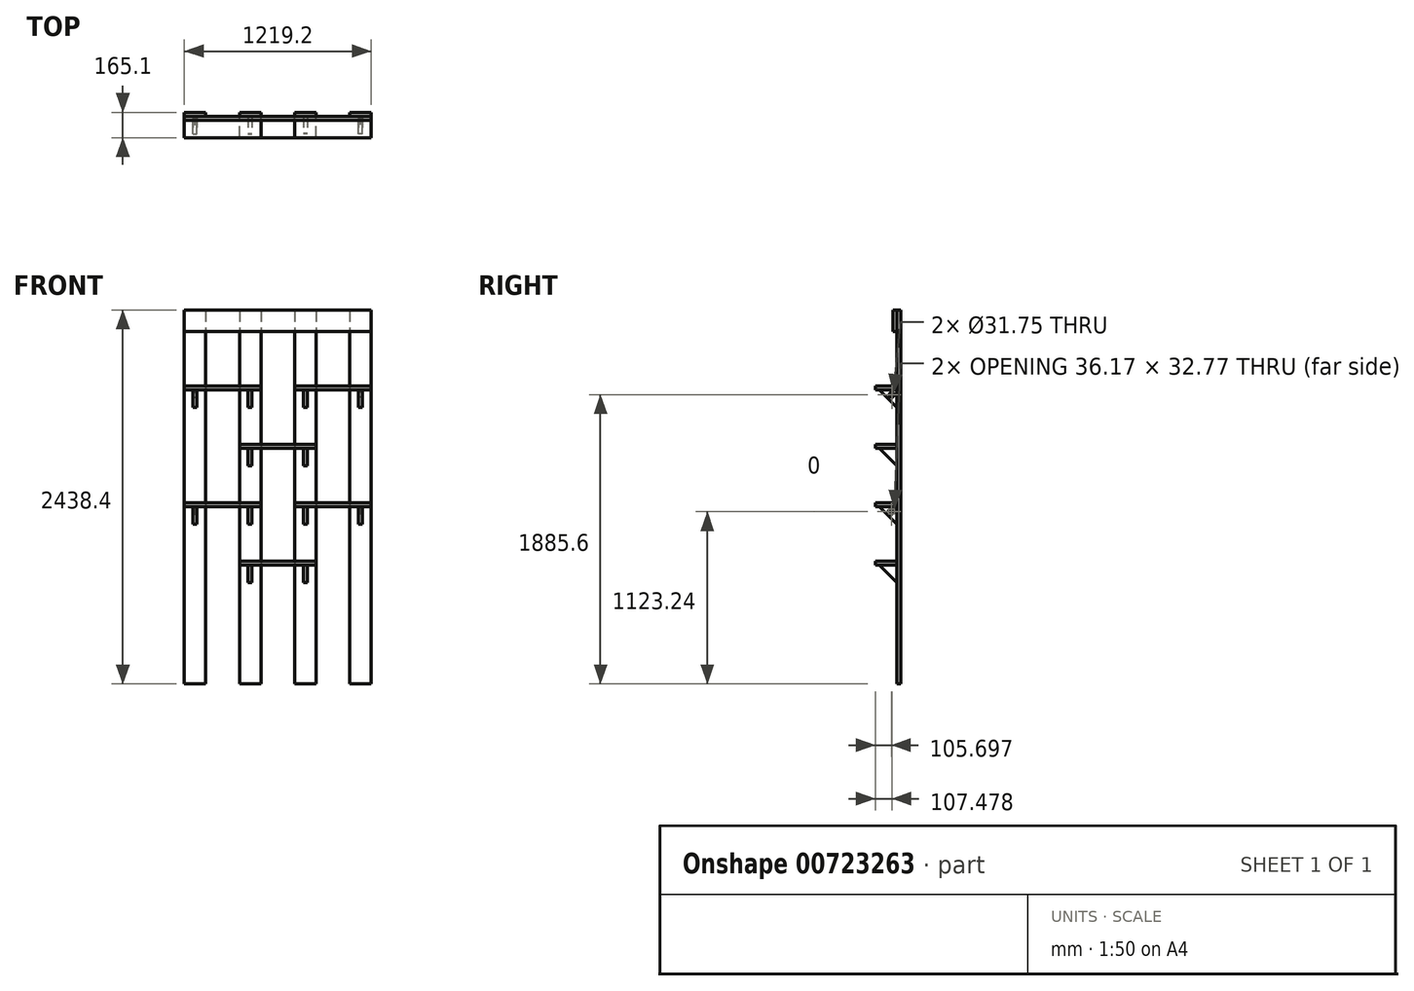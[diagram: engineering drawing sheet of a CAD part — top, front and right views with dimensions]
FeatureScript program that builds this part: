
annotation { "Feature Type Name" : "Feature", "Feature Type Description" : "" }
export const myFeature = defineFeature(function(context is Context, id is Id, definition is map)
    precondition{}
    {
        {
            var Q0;
            Q0=qCreatedBy(makeId("Front.planeOp"),FACE);
            var Q1;
            Q1 = qBodyType(qCreatedBy(id + "F1" ,EDGE), BodyType.WIRE);
            cPlane(context, id + "F0", {"entities" : qUnion([Q0, Q1]), "cplaneType" : CPlaneType.OFFSET, "offset" : 25.4 * mm, "width" : 152.4 * mm, "height" : 152.4 * mm});
        }
        {
            var Q0;
            Q0=qCreatedBy(id+"F0.planeOp",FACE);
            var sketch = newSketch(context, id + "F1", { "sketchPlane" : qUnion([Q0])});
            skLineSegment(sketch, "E0.bottom", {"start": v(-609.6, 139.7) * mm, "end": v(609.6, 139.7) * mm});
            skLineSegment(sketch, "E0.top", {"start": v(-609.6, 0) * mm, "end": v(609.6, 0) * mm});
            skLineSegment(sketch, "E0.left", {"start": v(-609.6, 139.7) * mm, "end": v(-609.6, 0) * mm});
            skLineSegment(sketch, "E0.right", {"start": v(609.6, 139.7) * mm, "end": v(609.6, 0) * mm});
            skPoint(sketch, "E1", {"position": v(0, 0) * mm});
            skSolve(sketch);
        }
        {
            var Q0;
            Q0=qCreatedBy(makeId("Front.planeOp"),FACE);
            var sketch = newSketch(context, id + "F2", { "sketchPlane" : qUnion([Q0])});
            skLineSegment(sketch, "E2.bottom", {"start": v(-609.6, 139.7) * mm, "end": v(-469.9, 139.7) * mm});
            skLineSegment(sketch, "E2.top", {"start": v(-609.6, -2298.7) * mm, "end": v(-469.9, -2298.7) * mm});
            skLineSegment(sketch, "E2.left", {"start": v(-609.6, 139.7) * mm, "end": v(-609.6, -2298.7) * mm});
            skLineSegment(sketch, "E2.right", {"start": v(-469.9, 139.7) * mm, "end": v(-469.9, -2298.7) * mm});
            skLineSegment(sketch, "E3", {"start": v(304.8, 139.7) * mm, "end": v(304.8, -1993.9) * mm, "construction": true});
            skLineSegment(sketch, "E4.MirrorCS", {"start": v(0.57, 139.7) * mm, "end": v(0.57, -1993.9) * mm, "construction": true});
            skLineSegment(sketch, "E5.bottom", {"start": v(110.24, 139.7) * mm, "end": v(249.94, 139.7) * mm});
            skLineSegment(sketch, "E5.top", {"start": v(110.24, -2298.7) * mm, "end": v(249.94, -2298.7) * mm});
            skLineSegment(sketch, "E5.left", {"start": v(110.24, 139.7) * mm, "end": v(110.24, -2298.7) * mm});
            skLineSegment(sketch, "E5.right", {"start": v(249.94, 139.7) * mm, "end": v(249.94, -2298.7) * mm});
            skLineSegment(sketch, "E6.bottom", {"start": v(469.9, 139.7) * mm, "end": v(609.6, 139.7) * mm});
            skLineSegment(sketch, "E6.top", {"start": v(469.9, -2298.7) * mm, "end": v(609.6, -2298.7) * mm});
            skLineSegment(sketch, "E6.left", {"start": v(469.9, 139.7) * mm, "end": v(469.9, -2298.7) * mm});
            skLineSegment(sketch, "E6.right", {"start": v(609.6, 139.7) * mm, "end": v(609.6, -2298.7) * mm});
            skLineSegment(sketch, "E7.bottom", {"start": v(-249.68, 139.7) * mm, "end": v(-109.98, 139.7) * mm});
            skLineSegment(sketch, "E7.top", {"start": v(-249.68, -2298.7) * mm, "end": v(-109.98, -2298.7) * mm});
            skLineSegment(sketch, "E7.left", {"start": v(-249.68, 139.7) * mm, "end": v(-249.68, -2298.7) * mm});
            skLineSegment(sketch, "E7.right", {"start": v(-109.98, 139.7) * mm, "end": v(-109.98, -2298.7) * mm});
            skLineSegment(sketch, "E8.0", {"start": v(-609.6, 139.7) * mm, "end": v(609.6, 139.7) * mm, "construction": true});
            skSolve(sketch);
        }
        {
            var Q0;
            Q0 = qSketchRegion(id + "F2", true);
            extrude(context, id + "F3", {"entities" : qUnion([Q0]), "depth" : 25.4 * mm, "offsetDistance" : 25.4 * mm});
        }
        {
            var Q0;
            Q0 = qSketchRegion(id + "F1", true);
            extrude(context, id + "F4", {"entities" : qUnion([Q0]), "depth" : 25.4 * mm, "offsetDistance" : 25.4 * mm});
        }
        {
            var Q0;
            Q0=makeQuery(id+"F3.opExtrude","CAP_FACE",FACE,{"disambiguationData":[OSD([sQuery(id+"F2.wireOp",EDGE,"E2.bottom"),sQuery(id+"F2.wireOp",EDGE,"E2.top"),sQuery(id+"F2.wireOp",EDGE,"E2.left"),sQuery(id+"F2.wireOp",EDGE,"E2.right")])],"isStart":false});
            var sketch = newSketch(context, id + "F5", { "sketchPlane" : qUnion([Q0])});
            skLineSegment(sketch, "E9.bottom", {"start": v(-609.6, -355.6) * mm, "end": v(-109.98, -355.6) * mm});
            skLineSegment(sketch, "E9.top", {"start": v(-609.6, -381) * mm, "end": v(-109.98, -381) * mm});
            skLineSegment(sketch, "E9.left", {"start": v(-609.6, -355.6) * mm, "end": v(-609.6, -381) * mm});
            skLineSegment(sketch, "E9.right", {"start": v(-109.98, -355.6) * mm, "end": v(-109.98, -381) * mm});
            skLineSegment(sketch, "E10.bottom", {"start": v(-249.68, -736.6) * mm, "end": v(249.94, -736.6) * mm});
            skLineSegment(sketch, "E10.top", {"start": v(-249.68, -762) * mm, "end": v(249.94, -762) * mm});
            skLineSegment(sketch, "E10.left", {"start": v(-249.68, -736.6) * mm, "end": v(-249.68, -762) * mm});
            skLineSegment(sketch, "E10.right", {"start": v(249.94, -736.6) * mm, "end": v(249.94, -762) * mm});
            skLineSegment(sketch, "E11.bottom", {"start": v(110.24, -355.6) * mm, "end": v(609.6, -355.6) * mm});
            skLineSegment(sketch, "E11.top", {"start": v(110.24, -381) * mm, "end": v(609.6, -381) * mm});
            skLineSegment(sketch, "E11.left", {"start": v(110.24, -355.6) * mm, "end": v(110.24, -381) * mm});
            skLineSegment(sketch, "E11.right", {"start": v(609.6, -355.6) * mm, "end": v(609.6, -381) * mm});
            skLineSegment(sketch, "E12.bottom", {"start": v(-609.6, -1117.6) * mm, "end": v(-109.98, -1117.6) * mm});
            skLineSegment(sketch, "E12.top", {"start": v(-609.6, -1143) * mm, "end": v(-109.98, -1143) * mm});
            skLineSegment(sketch, "E12.left", {"start": v(-609.6, -1117.6) * mm, "end": v(-609.6, -1143) * mm});
            skLineSegment(sketch, "E12.right", {"start": v(-109.98, -1117.6) * mm, "end": v(-109.98, -1143) * mm});
            skLineSegment(sketch, "E13.bottom", {"start": v(-249.68, -1498.6) * mm, "end": v(249.94, -1498.6) * mm});
            skLineSegment(sketch, "E13.top", {"start": v(-249.68, -1524) * mm, "end": v(249.94, -1524) * mm});
            skLineSegment(sketch, "E13.left", {"start": v(-249.68, -1498.6) * mm, "end": v(-249.68, -1524) * mm});
            skLineSegment(sketch, "E13.right", {"start": v(249.94, -1498.6) * mm, "end": v(249.94, -1524) * mm});
            skLineSegment(sketch, "E14.bottom", {"start": v(110.24, -1117.6) * mm, "end": v(609.6, -1117.6) * mm});
            skLineSegment(sketch, "E14.top", {"start": v(110.24, -1143) * mm, "end": v(609.6, -1143) * mm});
            skLineSegment(sketch, "E14.left", {"start": v(110.24, -1117.6) * mm, "end": v(110.24, -1143) * mm});
            skLineSegment(sketch, "E14.right", {"start": v(609.6, -1117.6) * mm, "end": v(609.6, -1143) * mm});
            skSolve(sketch);
        }
        {
            var Q0;
            Q0 = qSketchRegion(id + "F5", true);
            extrude(context, id + "F6", {"entities" : qUnion([Q0]), "depth" : 139.7 * mm, "offsetDistance" : 25.4 * mm});
        }
        {
            var Q0;
            Q0=qCreatedBy(makeId("Right.planeOp"),FACE);
            cPlane(context, id + "F7", {"entities" : qUnion([Q0]), "cplaneType" : CPlaneType.OFFSET, "offset" : 527.05 * mm, "width" : 152.4 * mm, "height" : 152.4 * mm});
        }
        {
            var Q0;
            Q0=qCreatedBy(id+"F7.planeOp",FACE);
            var sketch = newSketch(context, id + "F8", { "sketchPlane" : qUnion([Q0])});
            skLineSegment(sketch, "E15", {"start": v(-25.4, -495.3) * mm, "end": v(-139.7, -381) * mm});
            skLineSegment(sketch, "E16", {"start": v(-139.7, -381) * mm, "end": v(-25.69, -381) * mm});
            skLineSegment(sketch, "E17", {"start": v(-25.69, -381) * mm, "end": v(-25.4, -495.3) * mm});
            skLineSegment(sketch, "E18", {"start": v(-25.4, -1257.3) * mm, "end": v(-140.18, -1143) * mm});
            skLineSegment(sketch, "E19", {"start": v(-140.18, -1143) * mm, "end": v(-25.4, -1143) * mm});
            skLineSegment(sketch, "E20", {"start": v(-25.4, -1143) * mm, "end": v(-25.4, -1257.3) * mm});
            skLineSegment(sketch, "E21", {"start": v(-82.55, -438.15) * mm, "end": v(-25.69, -381) * mm, "construction": true});
            skCircle(sketch, "E22", {"center": v(-57.62, -413.1) * mm, "radius": 15.88 * mm});
            skLineSegment(sketch, "E23", {"start": v(-82.79, -1200.15) * mm, "end": v(-25.4, -1143) * mm, "construction": true});
            skCircle(sketch, "E24", {"center": v(-67.97, -1168.58) * mm, "radius": 9.53 * mm});
            skCircle(sketch, "E25", {"center": v(-50.84, -1168.71) * mm, "radius": 9.53 * mm});
            skCircle(sketch, "E26", {"center": v(-59.68, -1182.32) * mm, "radius": 9.53 * mm});
            skSolve(sketch);
        }
        {
            var Q0;
            Q0=makeQuery(id+"F8.imprint","IMPRINT",FACE,{"disambiguationData":[TD([[makeQuery(id+"F8.imprint","IMPRINT",EDGE,{"derivedFrom":sQuery(id+"F8.wireOp",EDGE,"E15")}),-1.0]])]});
            var Q1;
            Q1=makeQuery(id+"F8.imprint","IMPRINT",FACE,{"disambiguationData":[TD([[makeQuery(id+"F8.imprint","IMPRINT",EDGE,{"derivedFrom":sQuery(id+"F8.wireOp",EDGE,"E18")}),-1.0]])]});
            extrude(context, id + "F9", {"entities" : qUnion([Q0, Q1]), "depth" : 25.4 * mm, "offsetDistance" : 25.4 * mm});
        }
        {
            var Q0;
            Q0=qCreatedBy(makeId("Right.planeOp"),FACE);
            cPlane(context, id + "F10", {"entities" : qUnion([Q0]), "cplaneType" : CPlaneType.OFFSET, "offset" : 167.39 * mm, "width" : 152.4 * mm, "height" : 152.4 * mm});
        }
        {
            var Q0;
            Q0=qCreatedBy(id+"F10.planeOp",FACE);
            var sketch = newSketch(context, id + "F11", { "sketchPlane" : qUnion([Q0])});
            skLineSegment(sketch, "E27", {"start": v(-25.4, -495.3) * mm, "end": v(-139.43, -381) * mm});
            skLineSegment(sketch, "E28", {"start": v(-139.43, -381) * mm, "end": v(-25.4, -381) * mm});
            skLineSegment(sketch, "E29", {"start": v(-25.4, -381) * mm, "end": v(-25.4, -495.3) * mm});
            skLineSegment(sketch, "E30", {"start": v(-25.4, -1257.3) * mm, "end": v(-140.18, -1143) * mm});
            skLineSegment(sketch, "E31", {"start": v(-140.18, -1143) * mm, "end": v(-25.4, -1143) * mm});
            skLineSegment(sketch, "E32", {"start": v(-25.4, -1143) * mm, "end": v(-25.4, -1257.3) * mm});
            skLineSegment(sketch, "E33", {"start": v(-25.4, -876.3) * mm, "end": v(-139.14, -762) * mm});
            skLineSegment(sketch, "E34", {"start": v(-139.14, -762) * mm, "end": v(-25.4, -762) * mm});
            skLineSegment(sketch, "E35", {"start": v(-25.4, -762) * mm, "end": v(-25.4, -876.3) * mm});
            skLineSegment(sketch, "E36", {"start": v(-25.4, -1638.68) * mm, "end": v(-140.18, -1524) * mm});
            skLineSegment(sketch, "E37", {"start": v(-140.18, -1524) * mm, "end": v(-25.4, -1524) * mm});
            skLineSegment(sketch, "E38", {"start": v(-25.4, -1524) * mm, "end": v(-25.4, -1638.68) * mm});
            skSolve(sketch);
        }
        {
            var Q0;
            Q0 = qSketchRegion(id + "F11", true);
            extrude(context, id + "F12", {"entities" : qUnion([Q0]), "depth" : 25.4 * mm, "offsetDistance" : 25.4 * mm});
        }
        {
            var Q0;
            Q0=makeQuery(id+"F12.opExtrude","SWEPT_BODY",BODY,{"disambiguationData":[OSD([sQuery(id+"F11.wireOp",EDGE,"E27"),sQuery(id+"F11.wireOp",EDGE,"E28"),sQuery(id+"F11.wireOp",EDGE,"E29")])]});
            var Q1;
            Q1=makeQuery(id+"F9.opExtrude","SWEPT_BODY",BODY,{"disambiguationData":[OSD([sQuery(id+"F8.wireOp",EDGE,"E15"),sQuery(id+"F8.wireOp",EDGE,"E16"),sQuery(id+"F8.wireOp",EDGE,"E17")])]});
            var Q2;
            Q2=makeQuery(id+"F12.opExtrude","SWEPT_BODY",BODY,{"disambiguationData":[OSD([sQuery(id+"F11.wireOp",EDGE,"E33"),sQuery(id+"F11.wireOp",EDGE,"E34"),sQuery(id+"F11.wireOp",EDGE,"E35")])]});
            var Q3;
            Q3=makeQuery(id+"F12.opExtrude","SWEPT_BODY",BODY,{"disambiguationData":[OSD([sQuery(id+"F11.wireOp",EDGE,"E30"),sQuery(id+"F11.wireOp",EDGE,"E31"),sQuery(id+"F11.wireOp",EDGE,"E32")])]});
            var Q4;
            Q4=makeQuery(id+"F9.opExtrude","SWEPT_BODY",BODY,{"disambiguationData":[OSD([sQuery(id+"F8.wireOp",EDGE,"E18"),sQuery(id+"F8.wireOp",EDGE,"E19"),sQuery(id+"F8.wireOp",EDGE,"E20")])]});
            var Q5;
            Q5=makeQuery(id+"F12.opExtrude","SWEPT_BODY",BODY,{"disambiguationData":[OSD([sQuery(id+"F11.wireOp",EDGE,"E36"),sQuery(id+"F11.wireOp",EDGE,"E37"),sQuery(id+"F11.wireOp",EDGE,"E38")])]});
            var Q6;
            Q6=qCreatedBy(makeId("Right.planeOp"),FACE);
            mirror(context, id + "F13", {"entities" : qUnion([Q0, Q1, Q2, Q3, Q4, Q5]), "mirrorPlane" : qUnion([Q6])});
        }
    });
